# Revit family: LF6ALED
name_source: partatom
category: Lighting Fixtures
revit_build: Autodesk Revit 2014 (Build: 20130308_1515(x64)
units: mm (PartAtom-declared; Revit-internal decimal feet)

## types (1)
- LFA6ML
    Apparent Load = 0 VA
    Certifications = CSA certified to US and Canadian safety standards.
Suitable for damp locations. Approved for through
wiring. Non-IC rated
    Color Filter = 16777215
    Default Elevation = 48.000"
    Description = 6in Adjustable Luminaire
    Dimming Lamp Color Temperature Shift = <None>
    Emit Shape Visible in Rendering = No
    Emit from Circle Diameter = 7.000"
    Features = Light Engine utilizes Philips Fortimo LED module and provides controlled color consistency
All trims feature 35º vertical aiming and 362º rotational aiming
Universal 120-277V high efficiency LED driver with 0-10V dimming standard
67 Lumens per watt delivered
Glare free optical control
Shipped with pre-installed light commercial bar hangers. (see below for optional Commercial grade bar hangers)
Minimum 50,000 hours at 70% lumen maintenance
Photometrics tested per IESNA-LM-79-2008 standards
    Glass = Hubbell - White Glass
    Housing = Hubbell - Steel
    Input Power = 33 W
    Lamp = LED
    Load Classification = Lighting
    Manufacturer = Prescolite
    Model = LFA6ML
    Photometric Web File = LFA6SL-6LFASL15L30K8WFL45.IES
    Photometric Web Link = https://www.hubbell.com
    Product Documentation Link = https://hubbellcdn.com
    Product Page URL = https://www.hubbell.com
    Reflector = Hubbell - Aluminum
    Tilt Angle = -90.00°
    URL = http://www.prescolite.com
    Voltage = 120 V
    Warranty = 5 year warranty
    Wattage Comments = 32.7W

## geometry (parser evidence)
native form markers: Sweep x1
no freeform markers — native parametric forms only
